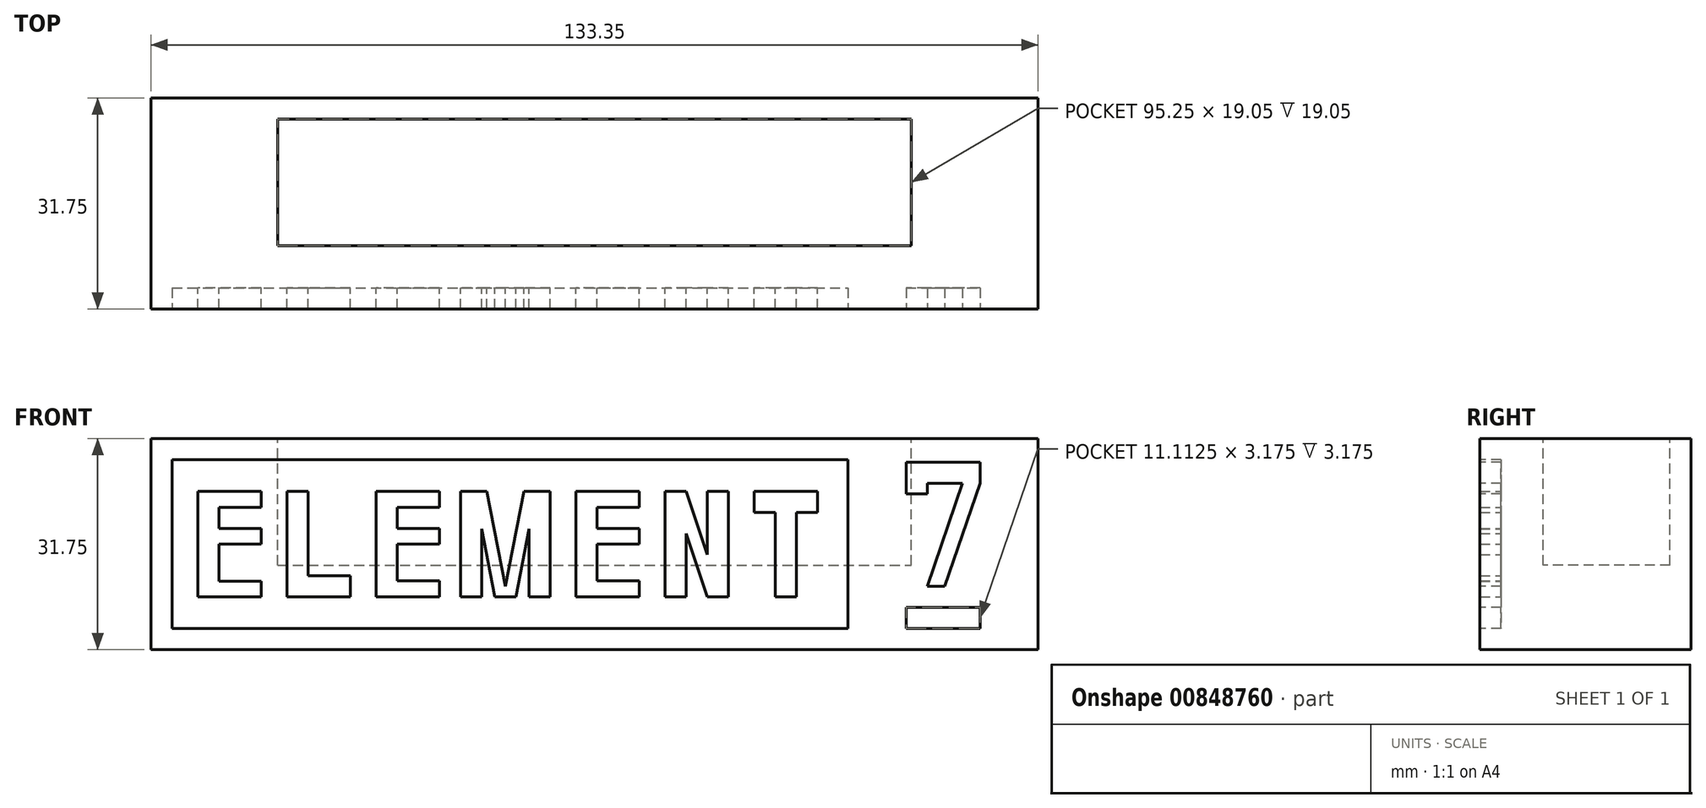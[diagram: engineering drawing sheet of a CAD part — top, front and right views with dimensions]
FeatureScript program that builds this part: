
annotation { "Feature Type Name" : "Feature", "Feature Type Description" : "" }
export const myFeature = defineFeature(function(context is Context, id is Id, definition is map)
    precondition{}
    {
        {
            var Q0;
            Q0=qCreatedBy(makeId("Front.planeOp"),FACE);
            var sketch = newSketch(context, id + "F0", { "sketchPlane" : qUnion([Q0])});
            skLineSegment(sketch, "E0.bottom", {"start": v(0, 0) * mm, "end": v(133.35, 0) * mm});
            skLineSegment(sketch, "E0.top", {"start": v(0, 31.75) * mm, "end": v(133.35, 31.75) * mm});
            skLineSegment(sketch, "E0.left", {"start": v(0, 0) * mm, "end": v(0, 31.75) * mm});
            skLineSegment(sketch, "E0.right", {"start": v(133.35, 0) * mm, "end": v(133.35, 31.75) * mm});
            skSolve(sketch);
        }
        {
            var Q0;
            Q0=makeQuery(id+"F0.imprint","IMPRINT",FACE,{"disambiguationData":[TD([[makeQuery(id+"F0.imprint","IMPRINT",EDGE,{"derivedFrom":sQuery(id+"F0.wireOp",EDGE,"E0.bottom")}),1.0]])]});
            extrude(context, id + "F1", {"entities" : qUnion([Q0]), "oppositeDirection" : true, "depth" : 31.75 * mm, "offsetDistance" : 25.4 * mm});
        }
        {
            var Q0;
            Q0=makeQuery(id+"F1.opExtrude","CAP_FACE",FACE,{"disambiguationData":[OSD([sQuery(id+"F0.wireOp",EDGE,"E0.bottom"),sQuery(id+"F0.wireOp",EDGE,"E0.top"),sQuery(id+"F0.wireOp",EDGE,"E0.left"),sQuery(id+"F0.wireOp",EDGE,"E0.right")])],"isStart":true});
            var sketch = newSketch(context, id + "F2", { "sketchPlane" : qUnion([Q0])});
            skLineSegment(sketch, "E1.bottom", {"start": v(3.17, 28.57) * mm, "end": v(104.78, 28.58) * mm});
            skLineSegment(sketch, "E1.top", {"start": v(3.18, 3.17) * mm, "end": v(104.78, 3.18) * mm});
            skLineSegment(sketch, "E1.left", {"start": v(3.17, 28.57) * mm, "end": v(3.18, 3.17) * mm});
            skLineSegment(sketch, "E1.right", {"start": v(104.78, 28.58) * mm, "end": v(104.78, 3.18) * mm});
            skSolve(sketch);
        }
        {
            var Q0;
            Q0=makeQuery(id+"F2.imprint","IMPRINT",FACE,{"disambiguationData":[TD([[makeQuery(id+"F2.imprint","IMPRINT",EDGE,{"derivedFrom":sQuery(id+"F2.wireOp",EDGE,"E1.bottom")}),-1.0]])]});
            extrude(context, id + "F3", {"entities" : qUnion([Q0]), "operationType" : NewBodyOperationType.REMOVE, "oppositeDirection" : true, "depth" : 3.17 * mm, "offsetDistance" : 25.4 * mm});
        }
        {
            var Q0;
            Q0=makeQuery(id+"F3.boolean.opBoolean","COPY",FACE,{"derivedFrom":makeQuery(id+"F3.opExtrude","CAP_FACE",FACE,{"disambiguationData":[OSD([sQuery(id+"F2.wireOp",EDGE,"E1.bottom"),sQuery(id+"F2.wireOp",EDGE,"E1.top"),sQuery(id+"F2.wireOp",EDGE,"E1.left"),sQuery(id+"F2.wireOp",EDGE,"E1.right")])],"isStart":false})});
            var sketch = newSketch(context, id + "F4", { "sketchPlane" : qUnion([Q0])});
            skLineSegment(sketch, "E2", {"start": v(7.05, 23.8) * mm, "end": v(7.05, 7.94) * mm});
            skLineSegment(sketch, "E3", {"start": v(7.05, 7.94) * mm, "end": v(16.57, 7.94) * mm});
            skLineSegment(sketch, "E4", {"start": v(16.57, 7.94) * mm, "end": v(16.57, 10.32) * mm});
            skLineSegment(sketch, "E5", {"start": v(16.57, 10.32) * mm, "end": v(10.22, 10.32) * mm});
            skLineSegment(sketch, "E6", {"start": v(10.22, 10.32) * mm, "end": v(10.22, 15.86) * mm});
            skLineSegment(sketch, "E7", {"start": v(10.22, 15.86) * mm, "end": v(16.57, 15.86) * mm});
            skLineSegment(sketch, "E8", {"start": v(16.57, 15.86) * mm, "end": v(16.57, 18.24) * mm});
            skLineSegment(sketch, "E9", {"start": v(16.57, 18.24) * mm, "end": v(10.22, 18.24) * mm});
            skLineSegment(sketch, "E10", {"start": v(10.22, 18.24) * mm, "end": v(10.22, 21.41) * mm});
            skLineSegment(sketch, "E11", {"start": v(10.22, 21.41) * mm, "end": v(16.57, 21.41) * mm});
            skLineSegment(sketch, "E12", {"start": v(16.57, 21.41) * mm, "end": v(16.57, 23.8) * mm});
            skLineSegment(sketch, "E13", {"start": v(16.57, 23.8) * mm, "end": v(7.05, 23.8) * mm});
            skSolve(sketch);
        }
        {
            var Q0;
            Q0=makeQuery(id+"F4.imprint","IMPRINT",FACE,{"disambiguationData":[TD([[makeQuery(id+"F4.imprint","IMPRINT",EDGE,{"derivedFrom":sQuery(id+"F4.wireOp",EDGE,"E2")}),1.0]])]});
            extrude(context, id + "F5", {"entities" : qUnion([Q0]), "operationType" : NewBodyOperationType.ADD, "depth" : 3.17 * mm, "offsetDistance" : 25.4 * mm});
        }
        {
            var Q0;
            Q0=makeQuery(id+"F1.opExtrude","CAP_FACE",FACE,{"disambiguationData":[OSD([sQuery(id+"F0.wireOp",EDGE,"E0.bottom"),sQuery(id+"F0.wireOp",EDGE,"E0.top"),sQuery(id+"F0.wireOp",EDGE,"E0.left"),sQuery(id+"F0.wireOp",EDGE,"E0.right")])],"isStart":true});
            var sketch = newSketch(context, id + "F6", { "sketchPlane" : qUnion([Q0])});
            skLineSegment(sketch, "E14.bottom", {"start": v(113.5, 3.18) * mm, "end": v(124.62, 3.18) * mm});
            skLineSegment(sketch, "E14.top", {"start": v(113.5, 6.35) * mm, "end": v(124.62, 6.35) * mm});
            skLineSegment(sketch, "E14.left", {"start": v(113.5, 3.17) * mm, "end": v(113.5, 6.35) * mm});
            skLineSegment(sketch, "E14.right", {"start": v(124.62, 3.18) * mm, "end": v(124.62, 6.35) * mm});
            skSolve(sketch);
        }
        {
            var Q0;
            Q0=makeQuery(id+"F6.imprint","IMPRINT",FACE,{"disambiguationData":[TD([[makeQuery(id+"F6.imprint","IMPRINT",EDGE,{"derivedFrom":sQuery(id+"F6.wireOp",EDGE,"E14.bottom")}),1.0]])]});
            extrude(context, id + "F7", {"entities" : qUnion([Q0]), "operationType" : NewBodyOperationType.REMOVE, "oppositeDirection" : true, "depth" : 3.17 * mm, "offsetDistance" : 25.4 * mm});
        }
        {
            var Q0;
            Q0=makeQuery(id+"F1.opExtrude","CAP_FACE",FACE,{"disambiguationData":[OSD([sQuery(id+"F0.wireOp",EDGE,"E0.bottom"),sQuery(id+"F0.wireOp",EDGE,"E0.top"),sQuery(id+"F0.wireOp",EDGE,"E0.left"),sQuery(id+"F0.wireOp",EDGE,"E0.right")])],"isStart":true});
            var sketch = newSketch(context, id + "F8", { "sketchPlane" : qUnion([Q0])});
            skLineSegment(sketch, "E15", {"start": v(113.5, 28.21) * mm, "end": v(124.62, 28.21) * mm});
            skLineSegment(sketch, "E16", {"start": v(124.62, 28.21) * mm, "end": v(124.62, 25.04) * mm});
            skLineSegment(sketch, "E17", {"start": v(124.62, 25.04) * mm, "end": v(119.33, 9.53) * mm});
            skLineSegment(sketch, "E18", {"start": v(119.33, 9.53) * mm, "end": v(116.68, 9.53) * mm});
            skLineSegment(sketch, "E19", {"start": v(116.68, 9.52) * mm, "end": v(121.97, 25.04) * mm});
            skPoint(sketch, "E19.endSnap0", {"position": v(121.97, 17.28) * mm});
            skLineSegment(sketch, "E20", {"start": v(121.97, 25.04) * mm, "end": v(116.68, 25.04) * mm});
            skLineSegment(sketch, "E21", {"start": v(116.68, 25.04) * mm, "end": v(116.68, 23.45) * mm});
            skLineSegment(sketch, "E22", {"start": v(116.68, 23.45) * mm, "end": v(113.5, 23.45) * mm});
            skLineSegment(sketch, "E23", {"start": v(113.5, 23.45) * mm, "end": v(113.5, 28.21) * mm});
            skSolve(sketch);
        }
        {
            var Q0;
            Q0=makeQuery(id+"F8.imprint","IMPRINT",FACE,{"disambiguationData":[TD([[makeQuery(id+"F8.imprint","IMPRINT",EDGE,{"derivedFrom":sQuery(id+"F8.wireOp",EDGE,"E15")}),-1.0]])]});
            extrude(context, id + "F9", {"entities" : qUnion([Q0]), "operationType" : NewBodyOperationType.REMOVE, "oppositeDirection" : true, "depth" : 3.17 * mm, "offsetDistance" : 25.4 * mm});
        }
        {
            var Q0;
            Q0=makeQuery(id+"F3.boolean.opBoolean","COPY",FACE,{"derivedFrom":makeQuery(id+"F3.opExtrude","CAP_FACE",FACE,{"disambiguationData":[OSD([sQuery(id+"F2.wireOp",EDGE,"E1.bottom"),sQuery(id+"F2.wireOp",EDGE,"E1.top"),sQuery(id+"F2.wireOp",EDGE,"E1.left"),sQuery(id+"F2.wireOp",EDGE,"E1.right")])],"isStart":false})});
            var sketch = newSketch(context, id + "F10", { "sketchPlane" : qUnion([Q0])});
            skLineSegment(sketch, "E24", {"start": v(20.44, 23.8) * mm, "end": v(20.44, 7.95) * mm});
            skLineSegment(sketch, "E25", {"start": v(20.44, 7.95) * mm, "end": v(29.97, 7.95) * mm});
            skLineSegment(sketch, "E26", {"start": v(29.97, 7.95) * mm, "end": v(29.97, 11.13) * mm});
            skLineSegment(sketch, "E27", {"start": v(29.97, 11.13) * mm, "end": v(23.62, 11.13) * mm});
            skLineSegment(sketch, "E28", {"start": v(23.62, 11.13) * mm, "end": v(23.62, 23.8) * mm});
            skLineSegment(sketch, "E29", {"start": v(23.62, 23.8) * mm, "end": v(20.44, 23.8) * mm});
            skSolve(sketch);
        }
        {
            var Q0;
            Q0=makeQuery(id+"F10.imprint","IMPRINT",FACE,{"disambiguationData":[TD([[makeQuery(id+"F10.imprint","IMPRINT",EDGE,{"derivedFrom":sQuery(id+"F10.wireOp",EDGE,"E24")}),1.0]])]});
            extrude(context, id + "F11", {"entities" : qUnion([Q0]), "operationType" : NewBodyOperationType.ADD, "depth" : 3.17 * mm, "offsetDistance" : 25.4 * mm});
        }
        {
            var Q0;
            Q0=makeQuery(id+"F3.boolean.opBoolean","COPY",FACE,{"derivedFrom":makeQuery(id+"F3.opExtrude","CAP_FACE",FACE,{"disambiguationData":[OSD([sQuery(id+"F2.wireOp",EDGE,"E1.bottom"),sQuery(id+"F2.wireOp",EDGE,"E1.top"),sQuery(id+"F2.wireOp",EDGE,"E1.left"),sQuery(id+"F2.wireOp",EDGE,"E1.right")])],"isStart":false})});
            var sketch = newSketch(context, id + "F12", { "sketchPlane" : qUnion([Q0])});
            skLineSegment(sketch, "E30", {"start": v(46.54, 23.8) * mm, "end": v(46.54, 7.95) * mm});
            skLineSegment(sketch, "E31", {"start": v(46.54, 7.95) * mm, "end": v(49.71, 7.95) * mm});
            skLineSegment(sketch, "E32", {"start": v(49.71, 7.95) * mm, "end": v(49.71, 18.15) * mm});
            skLineSegment(sketch, "E33", {"start": v(49.71, 18.15) * mm, "end": v(51.7, 7.95) * mm});
            skLineSegment(sketch, "E34", {"start": v(51.7, 7.95) * mm, "end": v(54.87, 7.95) * mm});
            skLineSegment(sketch, "E35", {"start": v(54.87, 7.95) * mm, "end": v(56.85, 18.15) * mm});
            skLineSegment(sketch, "E36", {"start": v(56.85, 18.15) * mm, "end": v(56.85, 7.95) * mm});
            skLineSegment(sketch, "E37", {"start": v(56.85, 7.95) * mm, "end": v(60.03, 7.95) * mm});
            skLineSegment(sketch, "E38", {"start": v(60.03, 7.95) * mm, "end": v(60.03, 23.8) * mm});
            skLineSegment(sketch, "E39", {"start": v(60.03, 23.8) * mm, "end": v(56.06, 23.8) * mm});
            skLineSegment(sketch, "E40", {"start": v(56.06, 23.8) * mm, "end": v(53.28, 9.53) * mm});
            skLineSegment(sketch, "E41", {"start": v(53.28, 9.53) * mm, "end": v(50.5, 23.8) * mm});
            skLineSegment(sketch, "E42", {"start": v(50.5, 23.8) * mm, "end": v(46.54, 23.8) * mm});
            skSolve(sketch);
        }
        {
            var Q0;
            Q0=makeQuery(id+"F12.imprint","IMPRINT",FACE,{"disambiguationData":[TD([[makeQuery(id+"F12.imprint","IMPRINT",EDGE,{"derivedFrom":sQuery(id+"F12.wireOp",EDGE,"E30")}),-1.0]])]});
            var sketch = newSketch(context, id + "F13", { "sketchPlane" : qUnion([Q0])});
            skLineSegment(sketch, "E43", {"start": v(33.84, 23.8) * mm, "end": v(33.84, 7.95) * mm});
            skLineSegment(sketch, "E44", {"start": v(33.84, 7.95) * mm, "end": v(43.36, 7.95) * mm});
            skLineSegment(sketch, "E45", {"start": v(43.36, 7.95) * mm, "end": v(43.36, 10.34) * mm});
            skLineSegment(sketch, "E46", {"start": v(43.36, 10.34) * mm, "end": v(37.01, 10.34) * mm});
            skLineSegment(sketch, "E47", {"start": v(37.01, 10.34) * mm, "end": v(37.01, 15.85) * mm});
            skLineSegment(sketch, "E48", {"start": v(37.01, 15.85) * mm, "end": v(43.36, 15.85) * mm});
            skLineSegment(sketch, "E49", {"start": v(43.36, 15.85) * mm, "end": v(43.36, 18.24) * mm});
            skLineSegment(sketch, "E50", {"start": v(43.36, 18.24) * mm, "end": v(37.01, 18.24) * mm});
            skLineSegment(sketch, "E51", {"start": v(37.01, 18.24) * mm, "end": v(37.01, 21.41) * mm});
            skLineSegment(sketch, "E52", {"start": v(37.01, 21.41) * mm, "end": v(43.36, 21.41) * mm});
            skLineSegment(sketch, "E53", {"start": v(43.36, 21.41) * mm, "end": v(43.36, 23.8) * mm});
            skLineSegment(sketch, "E54", {"start": v(43.36, 23.8) * mm, "end": v(33.84, 23.8) * mm});
            skSolve(sketch);
        }
        {
            var Q0;
            Q0=makeQuery(id+"F13.imprint","IMPRINT",FACE,{"disambiguationData":[TD([[makeQuery(id+"F13.imprint","IMPRINT",EDGE,{"derivedFrom":sQuery(id+"F13.wireOp",EDGE,"E43")}),1.0]])]});
            extrude(context, id + "F14", {"entities" : qUnion([Q0]), "operationType" : NewBodyOperationType.ADD, "depth" : 3.17 * mm, "offsetDistance" : 25.4 * mm});
        }
        {
            var Q0;
            Q0=makeQuery(id+"F12.imprint","IMPRINT",FACE,{"disambiguationData":[TD([[makeQuery(id+"F12.imprint","IMPRINT",EDGE,{"derivedFrom":sQuery(id+"F12.wireOp",EDGE,"E30")}),1.0]])]});
            extrude(context, id + "F15", {"entities" : qUnion([Q0]), "operationType" : NewBodyOperationType.ADD, "depth" : 3.17 * mm, "offsetDistance" : 25.4 * mm});
        }
        {
            var Q0;
            Q0=makeQuery(id+"F3.boolean.opBoolean","COPY",FACE,{"derivedFrom":makeQuery(id+"F3.opExtrude","CAP_FACE",FACE,{"disambiguationData":[OSD([sQuery(id+"F2.wireOp",EDGE,"E1.bottom"),sQuery(id+"F2.wireOp",EDGE,"E1.top"),sQuery(id+"F2.wireOp",EDGE,"E1.left"),sQuery(id+"F2.wireOp",EDGE,"E1.right")])],"isStart":false})});
            var sketch = newSketch(context, id + "F16", { "sketchPlane" : qUnion([Q0])});
            skLineSegment(sketch, "E55", {"start": v(63.9, 23.8) * mm, "end": v(63.9, 7.95) * mm});
            skLineSegment(sketch, "E56", {"start": v(63.9, 7.95) * mm, "end": v(73.43, 7.95) * mm});
            skLineSegment(sketch, "E57", {"start": v(73.43, 7.95) * mm, "end": v(73.43, 10.34) * mm});
            skLineSegment(sketch, "E58", {"start": v(73.43, 10.34) * mm, "end": v(67.08, 10.34) * mm});
            skLineSegment(sketch, "E59", {"start": v(67.08, 10.34) * mm, "end": v(67.08, 15.85) * mm});
            skLineSegment(sketch, "E60", {"start": v(67.08, 15.85) * mm, "end": v(73.43, 15.85) * mm});
            skLineSegment(sketch, "E61", {"start": v(73.43, 15.85) * mm, "end": v(73.43, 18.24) * mm});
            skLineSegment(sketch, "E62", {"start": v(73.43, 18.24) * mm, "end": v(67.08, 18.24) * mm});
            skLineSegment(sketch, "E63", {"start": v(67.08, 18.24) * mm, "end": v(67.08, 21.41) * mm});
            skLineSegment(sketch, "E64", {"start": v(67.08, 21.41) * mm, "end": v(73.43, 21.41) * mm});
            skLineSegment(sketch, "E65", {"start": v(73.43, 21.41) * mm, "end": v(73.43, 23.8) * mm});
            skLineSegment(sketch, "E66", {"start": v(73.43, 23.8) * mm, "end": v(63.9, 23.8) * mm});
            skSolve(sketch);
        }
        {
            var Q0;
            Q0=makeQuery(id+"F16.imprint","IMPRINT",FACE,{"disambiguationData":[TD([[makeQuery(id+"F16.imprint","IMPRINT",EDGE,{"derivedFrom":sQuery(id+"F16.wireOp",EDGE,"E55")}),1.0]])]});
            extrude(context, id + "F17", {"entities" : qUnion([Q0]), "operationType" : NewBodyOperationType.ADD, "depth" : 3.17 * mm, "offsetDistance" : 25.4 * mm});
        }
        {
            var Q0;
            Q0=makeQuery(id+"F3.boolean.opBoolean","COPY",FACE,{"derivedFrom":makeQuery(id+"F3.opExtrude","CAP_FACE",FACE,{"disambiguationData":[OSD([sQuery(id+"F2.wireOp",EDGE,"E1.bottom"),sQuery(id+"F2.wireOp",EDGE,"E1.top"),sQuery(id+"F2.wireOp",EDGE,"E1.left"),sQuery(id+"F2.wireOp",EDGE,"E1.right")])],"isStart":false})});
            var sketch = newSketch(context, id + "F18", { "sketchPlane" : qUnion([Q0])});
            skLineSegment(sketch, "E67", {"start": v(77.3, 23.8) * mm, "end": v(77.3, 7.95) * mm});
            skLineSegment(sketch, "E68", {"start": v(77.3, 7.95) * mm, "end": v(80.47, 7.95) * mm});
            skLineSegment(sketch, "E69", {"start": v(80.47, 7.95) * mm, "end": v(80.47, 17.48) * mm});
            skLineSegment(sketch, "E70", {"start": v(80.47, 17.48) * mm, "end": v(83.65, 7.95) * mm});
            skLineSegment(sketch, "E71", {"start": v(83.65, 7.95) * mm, "end": v(86.82, 7.95) * mm});
            skLineSegment(sketch, "E72", {"start": v(86.82, 7.95) * mm, "end": v(86.82, 23.8) * mm});
            skLineSegment(sketch, "E73", {"start": v(86.82, 23.8) * mm, "end": v(83.65, 23.8) * mm});
            skLineSegment(sketch, "E74", {"start": v(83.65, 23.8) * mm, "end": v(83.65, 14.27) * mm});
            skLineSegment(sketch, "E75", {"start": v(83.65, 14.27) * mm, "end": v(80.47, 23.8) * mm});
            skLineSegment(sketch, "E76", {"start": v(80.47, 23.8) * mm, "end": v(77.3, 23.8) * mm});
            skSolve(sketch);
        }
        {
            var Q0;
            Q0=makeQuery(id+"F18.imprint","IMPRINT",FACE,{"disambiguationData":[TD([[makeQuery(id+"F18.imprint","IMPRINT",EDGE,{"derivedFrom":sQuery(id+"F18.wireOp",EDGE,"E67")}),1.0]])]});
            extrude(context, id + "F19", {"entities" : qUnion([Q0]), "operationType" : NewBodyOperationType.ADD, "depth" : 3.17 * mm, "offsetDistance" : 25.4 * mm});
        }
        {
            var Q0;
            Q0=makeQuery(id+"F3.boolean.opBoolean","COPY",FACE,{"derivedFrom":makeQuery(id+"F3.opExtrude","CAP_FACE",FACE,{"disambiguationData":[OSD([sQuery(id+"F2.wireOp",EDGE,"E1.bottom"),sQuery(id+"F2.wireOp",EDGE,"E1.top"),sQuery(id+"F2.wireOp",EDGE,"E1.left"),sQuery(id+"F2.wireOp",EDGE,"E1.right")])],"isStart":false})});
            var sketch = newSketch(context, id + "F20", { "sketchPlane" : qUnion([Q0])});
            skLineSegment(sketch, "E77", {"start": v(90.7, 23.8) * mm, "end": v(100.22, 23.8) * mm});
            skLineSegment(sketch, "E78", {"start": v(100.22, 23.8) * mm, "end": v(100.22, 20.62) * mm});
            skLineSegment(sketch, "E79", {"start": v(100.22, 20.62) * mm, "end": v(97.04, 20.62) * mm});
            skLineSegment(sketch, "E80", {"start": v(97.04, 20.62) * mm, "end": v(97.04, 7.95) * mm});
            skLineSegment(sketch, "E81", {"start": v(97.04, 7.95) * mm, "end": v(93.87, 7.95) * mm});
            skLineSegment(sketch, "E82", {"start": v(93.87, 7.95) * mm, "end": v(93.87, 20.62) * mm});
            skLineSegment(sketch, "E83", {"start": v(93.87, 20.62) * mm, "end": v(90.7, 20.62) * mm});
            skLineSegment(sketch, "E84", {"start": v(90.7, 20.62) * mm, "end": v(90.7, 23.8) * mm});
            skSolve(sketch);
        }
        {
            var Q0;
            Q0 = qSketchRegion(id + "F20", true);
            extrude(context, id + "F21", {"entities" : qUnion([Q0]), "operationType" : NewBodyOperationType.ADD, "depth" : 3.17 * mm, "offsetDistance" : 25.4 * mm});
        }
        {
            var Q0;
            Q0=makeQuery(id+"F1.opExtrude","SWEPT_FACE",FACE,{"disambiguationData":[OSD([sQuery(id+"F0.wireOp",EDGE,"E0.top")])]});
            var sketch = newSketch(context, id + "F22", { "sketchPlane" : qUnion([Q0])});
            skLineSegment(sketch, "E85.bottom", {"start": v(19.05, 28.57) * mm, "end": v(114.3, 28.57) * mm});
            skLineSegment(sketch, "E85.top", {"start": v(19.05, 9.53) * mm, "end": v(114.3, 9.53) * mm});
            skLineSegment(sketch, "E85.left", {"start": v(19.05, 28.57) * mm, "end": v(19.05, 9.53) * mm});
            skLineSegment(sketch, "E85.right", {"start": v(114.3, 28.57) * mm, "end": v(114.3, 9.53) * mm});
            skSolve(sketch);
        }
        {
            var Q0;
            Q0=makeQuery(id+"F22.imprint","IMPRINT",FACE,{"disambiguationData":[TD([[makeQuery(id+"F22.imprint","IMPRINT",EDGE,{"derivedFrom":sQuery(id+"F22.wireOp",EDGE,"E85.bottom")}),-1.0]])]});
            extrude(context, id + "F23", {"entities" : qUnion([Q0]), "operationType" : NewBodyOperationType.REMOVE, "oppositeDirection" : true, "depth" : 19.05 * mm, "offsetDistance" : 25.4 * mm});
        }
    });
